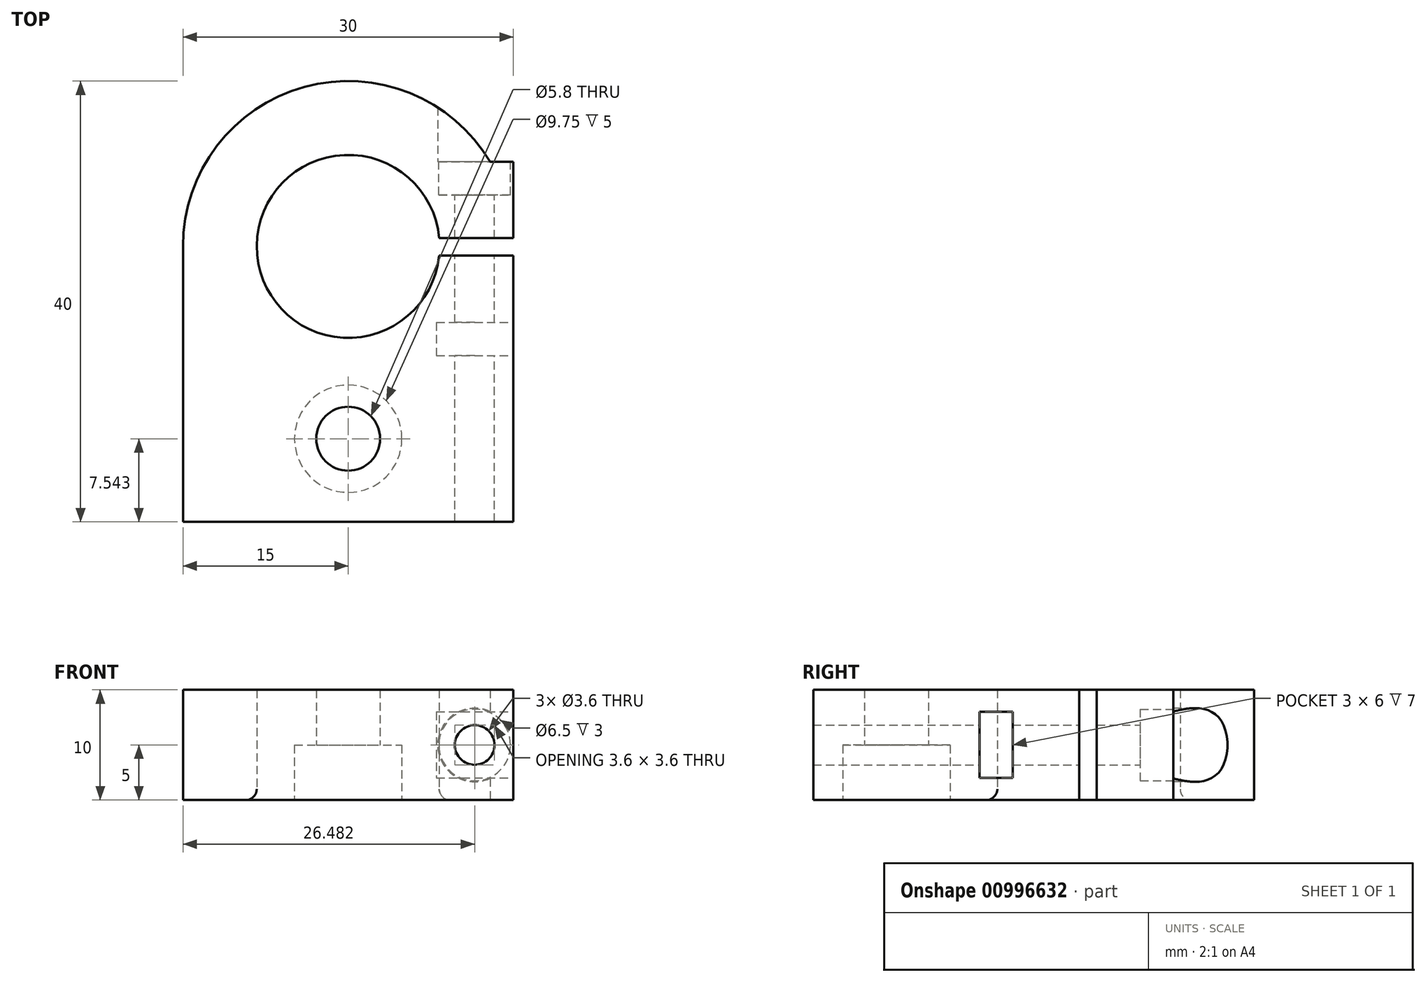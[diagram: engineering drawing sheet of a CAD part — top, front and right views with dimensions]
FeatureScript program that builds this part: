
annotation { "Feature Type Name" : "Feature", "Feature Type Description" : "" }
export const myFeature = defineFeature(function(context is Context, id is Id, definition is map)
    precondition{}
    {
        {
            var Q0;
            Q0=qCreatedBy(makeId("Top.planeOp"),FACE);
            var sketch = newSketch(context, id + "F0", { "sketchPlane" : qUnion([Q0])});
            skLineSegment(sketch, "E0.top", {"start": v(-15, -12.5) * mm, "end": v(15, -12.5) * mm});
            skLineSegment(sketch, "E0.left", {"start": v(-15, 12.5) * mm, "end": v(-15, -12.5) * mm});
            skLineSegment(sketch, "E0.right", {"start": v(15, 11.65) * mm, "end": v(15, -12.5) * mm});
            skPoint(sketch, "E0.middle", {"position": v(0, 0) * mm});
            skArc(sketch, "E1", {"start": v(12.89, 20.17) * mm, "mid": v(-3.98, 26.96) * mm, "end": v(-15, 12.5) * mm});
            skArc(sketch, "E2", {"start": v(8.27, 13.24) * mm, "mid": v(-8.3, 12.56) * mm, "end": v(8.26, 11.65) * mm});
            skLineSegment(sketch, "E3.bottom", {"start": v(8.27, 13.24) * mm, "end": v(14.98, 13.24) * mm});
            skLineSegment(sketch, "E3.top", {"start": v(8.26, 11.65) * mm, "end": v(15, 11.65) * mm});
            skPoint(sketch, "E4.orphan", {"position": v(15, 12.5) * mm});
            skLineSegment(sketch, "E5", {"start": v(14.98, 13.24) * mm, "end": v(14.98, 20.17) * mm});
            skLineSegment(sketch, "E6", {"start": v(14.98, 20.17) * mm, "end": v(12.89, 20.17) * mm});
            skSolve(sketch);
        }
        {
            var Q0;
            Q0=makeQuery(id+"F0.imprint","IMPRINT",FACE,{"disambiguationData":[TD([[makeQuery(id+"F0.imprint","IMPRINT",EDGE,{"derivedFrom":sQuery(id+"F0.wireOp",EDGE,"E0.top")}),1.0]])]});
            extrude(context, id + "F1", {"entities" : qUnion([Q0]), "depth" : 10 * mm, "offsetDistance" : 25 * mm});
        }
        {
            var Q0;
            Q0=makeQuery(id+"F1.opExtrude","CAP_FACE",FACE,{"disambiguationData":[OSD([sQuery(id+"F0.wireOp",EDGE,"E0.top"),sQuery(id+"F0.wireOp",EDGE,"E0.left"),sQuery(id+"F0.wireOp",EDGE,"E0.right"),sQuery(id+"F0.wireOp",EDGE,"E1"),sQuery(id+"F0.wireOp",EDGE,"E2"),sQuery(id+"F0.wireOp",EDGE,"E3.bottom"),sQuery(id+"F0.wireOp",EDGE,"E3.top"),sQuery(id+"F0.wireOp",EDGE,"E5"),sQuery(id+"F0.wireOp",EDGE,"E6")])],"isStart":true});
            var sketch = newSketch(context, id + "F2", { "sketchPlane" : qUnion([Q0])});
            skPoint(sketch, "E7", {"position": v(0, 4.96) * mm});
            skSolve(sketch);
        }
        {
            var Q0;
            Q0=sQuery(id+"F2.wireOp",VERTEX,"E7");
            var Q1;
            Q1=makeQuery(id+"F1.opExtrude","SWEPT_BODY",BODY,{"disambiguationData":[OSD([sQuery(id+"F0.wireOp",EDGE,"E0.top"),sQuery(id+"F0.wireOp",EDGE,"E0.left"),sQuery(id+"F0.wireOp",EDGE,"E0.right"),sQuery(id+"F0.wireOp",EDGE,"E1"),sQuery(id+"F0.wireOp",EDGE,"E2"),sQuery(id+"F0.wireOp",EDGE,"E3.bottom"),sQuery(id+"F0.wireOp",EDGE,"E3.top"),sQuery(id+"F0.wireOp",EDGE,"E5"),sQuery(id+"F0.wireOp",EDGE,"E6")])]});
            hole(context, id + "F3", {"style" : HoleStyle.C_BORE, "endStyle" : HoleEndStyle.THROUGH, "standardTappedOrClearance" : lookupTablePath({ "fit" : "Loose", "standard" : "ISO", "size" : "M5", "type" : "Clearance" }), "standardBlindInLast" : lookupTablePath({ "fit" : "Loose", "standard" : "ISO", "engagement" : "75%", "pitch" : "0.8 mm", "size" : "M5", "type" : "Clearance & tapped" }), "holeDiameter" : 5.8 * mm, "cBoreDiameter" : 9.75 * mm, "cBoreDepth" : 5 * mm, "majorDiameter" : 5 * mm, "isTappedThrough" : true, "tappedDepth" : 12 * mm, "tapClearance" : 3, "locations" : qUnion([Q0]), "scope" : qUnion([Q1])});
        }
        {
            var Q0;
            Q0=makeQuery(id+"F1.opExtrude","SWEPT_FACE",FACE,{"disambiguationData":[OSD([sQuery(id+"F0.wireOp",EDGE,"E6")])]});
            var sketch = newSketch(context, id + "F4", { "sketchPlane" : qUnion([Q0])});
            skLineSegment(sketch, "E8", {"start": v(-14.98, 5) * mm, "end": v(27.88, 5) * mm, "construction": true});
            skPoint(sketch, "E9", {"position": v(-11.48, 5) * mm});
            skCircle(sketch, "E10", {"center": v(-11.48, 5) * mm, "radius": 3.34 * mm});
            skSolve(sketch);
        }
        {
            var Q0;
            Q0 = qSketchRegion(id + "F4", true);
            extrude(context, id + "F5", {"entities" : qUnion([Q0]), "operationType" : NewBodyOperationType.REMOVE, "depth" : 25 * mm, "offsetDistance" : 25 * mm});
        }
        {
            var Q0;
            Q0=sQuery(id+"F4.wireOp",VERTEX,"E9");
            var Q1;
            Q1=makeQuery(id+"F1.opExtrude","SWEPT_BODY",BODY,{"disambiguationData":[OSD([sQuery(id+"F0.wireOp",EDGE,"E0.top"),sQuery(id+"F0.wireOp",EDGE,"E0.left"),sQuery(id+"F0.wireOp",EDGE,"E0.right"),sQuery(id+"F0.wireOp",EDGE,"E1"),sQuery(id+"F0.wireOp",EDGE,"E2"),sQuery(id+"F0.wireOp",EDGE,"E3.bottom"),sQuery(id+"F0.wireOp",EDGE,"E3.top"),sQuery(id+"F0.wireOp",EDGE,"E5"),sQuery(id+"F0.wireOp",EDGE,"E6")])]});
            hole(context, id + "F6", {"style" : HoleStyle.C_BORE, "endStyle" : HoleEndStyle.THROUGH, "standardTappedOrClearance" : lookupTablePath({ "fit" : "Loose", "standard" : "ISO", "size" : "M3", "type" : "Clearance" }), "standardBlindInLast" : lookupTablePath({ "fit" : "Loose", "standard" : "ISO", "engagement" : "75%", "pitch" : "0.5 mm", "size" : "M3", "type" : "Clearance & tapped" }), "holeDiameter" : 3.6 * mm, "cBoreDiameter" : 6.5 * mm, "cBoreDepth" : 3 * mm, "majorDiameter" : 5 * mm, "isTappedThrough" : true, "tappedDepth" : 12 * mm, "tapClearance" : 3, "locations" : qUnion([Q0]), "scope" : qUnion([Q1])});
        }
        {
            var Q0;
            Q0=makeQuery(id+"F1.opExtrude","SWEPT_FACE",FACE,{"disambiguationData":[OSD([sQuery(id+"F0.wireOp",EDGE,"E0.right")])]});
            var sketch = newSketch(context, id + "F7", { "sketchPlane" : qUnion([Q0])});
            skLineSegment(sketch, "E11.bottom", {"start": v(5.6, 8) * mm, "end": v(2.6, 8) * mm});
            skLineSegment(sketch, "E11.top", {"start": v(5.6, 2) * mm, "end": v(2.6, 2) * mm});
            skLineSegment(sketch, "E11.left", {"start": v(5.6, 8) * mm, "end": v(5.6, 2) * mm});
            skLineSegment(sketch, "E11.right", {"start": v(2.6, 8) * mm, "end": v(2.6, 2) * mm});
            skPoint(sketch, "E11.middle", {"position": v(4.1, 5) * mm});
            skPoint(sketch, "E11.middle.positionSnap0", {"position": v(11.65, 5) * mm});
            skPoint(sketch, "E11.centerSnap0", {"position": v(11.65, 5) * mm});
            skSolve(sketch);
        }
        {
            var Q0;
            Q0=makeQuery(id+"F7.imprint","IMPRINT",FACE,{"disambiguationData":[TD([[makeQuery(id+"F7.imprint","IMPRINT",EDGE,{"derivedFrom":sQuery(id+"F7.wireOp",EDGE,"E11.bottom")}),1.0]])]});
            extrude(context, id + "F8", {"entities" : qUnion([Q0]), "operationType" : NewBodyOperationType.REMOVE, "oppositeDirection" : true, "depth" : 7 * mm, "offsetDistance" : 25 * mm});
        }
        {
            var Q0;
            Q0=makeQuery(id+"F1.opExtrude","CAP_EDGE",EDGE,{"disambiguationData":[OSD([sQuery(id+"F0.wireOp",EDGE,"E2")])],"isStart":true});
            fillet(context, id + "F9", {"entities" : qUnion([Q0]), "radius" : 1 * mm, "tangentPropagation" : true, "allowEdgeOverflow" : false});
        }
    });
